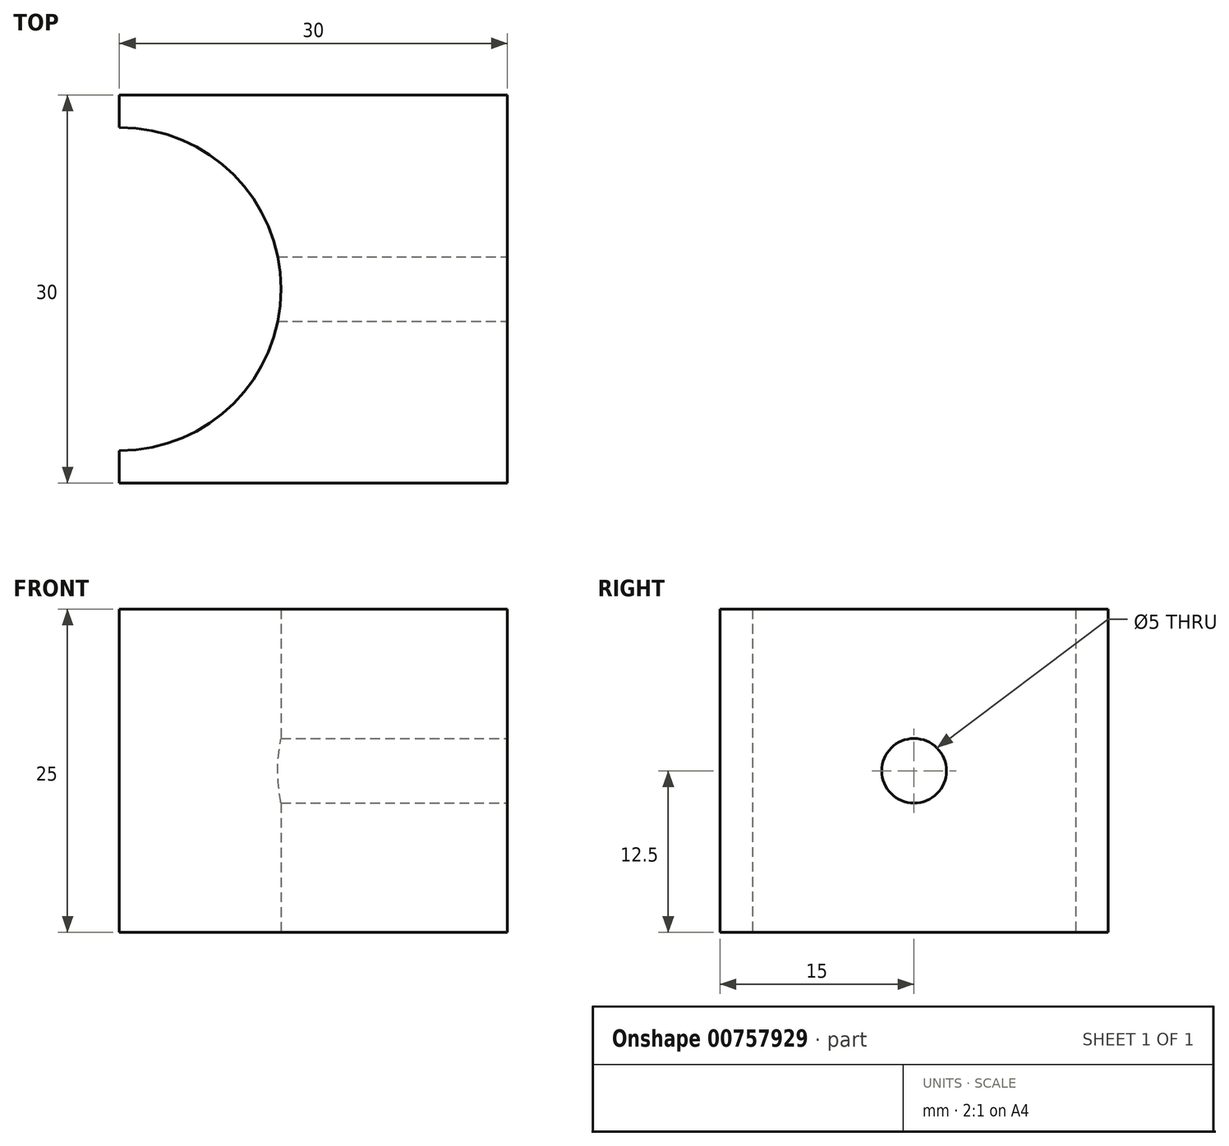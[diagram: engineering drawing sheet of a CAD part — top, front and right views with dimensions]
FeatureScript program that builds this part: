
annotation { "Feature Type Name" : "Feature", "Feature Type Description" : "" }
export const myFeature = defineFeature(function(context is Context, id is Id, definition is map)
    precondition{}
    {
        {
            var Q0;
            Q0=qCreatedBy(makeId("Top.planeOp"),FACE);
            var sketch = newSketch(context, id + "F0", { "sketchPlane" : qUnion([Q0])});
            skArc(sketch, "E0", {"start": v(0, -12.5) * mm, "mid": v(12.5, 0) * mm, "end": v(0, 12.5) * mm});
            skLineSegment(sketch, "E1", {"start": v(0, 15) * mm, "end": v(30, 15) * mm});
            skLineSegment(sketch, "E2", {"start": v(30, 15) * mm, "end": v(30, -15) * mm});
            skLineSegment(sketch, "E3", {"start": v(0, -15) * mm, "end": v(30, -15) * mm});
            skLineSegment(sketch, "E4", {"start": v(0, 15) * mm, "end": v(0, 12.5) * mm});
            skLineSegment(sketch, "E5", {"start": v(0, -15) * mm, "end": v(0, -12.5) * mm});
            skSolve(sketch);
        }
        {
            var Q0;
            Q0 = qSketchRegion(id + "F0", true);
            extrude(context, id + "F1", {"entities" : qUnion([Q0]), "depth" : 25 * mm, "offsetDistance" : 25 * mm});
        }
        {
            var Q0;
            Q0=makeQuery(id+"F1.opExtrude","SWEPT_FACE",FACE,{"disambiguationData":[OSD([sQuery(id+"F0.wireOp",EDGE,"E2")])]});
            var sketch = newSketch(context, id + "F2", { "sketchPlane" : qUnion([Q0])});
            skLineSegment(sketch, "E6", {"start": v(15, 25) * mm, "end": v(-15, 0) * mm, "construction": true});
            skPoint(sketch, "E7", {"position": v(0, 12.5) * mm});
            skSolve(sketch);
        }
        {
            var Q0;
            Q0=sQuery(id+"F2.wireOp",VERTEX,"E7");
            var Q1;
            Q1=makeQuery(id+"F1.opExtrude","SWEPT_BODY",BODY,{"disambiguationData":[OSD([sQuery(id+"F0.wireOp",EDGE,"E0"),sQuery(id+"F0.wireOp",EDGE,"E1"),sQuery(id+"F0.wireOp",EDGE,"E2"),sQuery(id+"F0.wireOp",EDGE,"E3"),sQuery(id+"F0.wireOp",EDGE,"E4"),sQuery(id+"F0.wireOp",EDGE,"E5")])]});
            hole(context, id + "F3", {"style" : HoleStyle.SIMPLE, "endStyle" : HoleEndStyle.THROUGH, "standardTappedOrClearance" : lookupTablePath({ "standard" : "ISO", "size" : "5", "type" : "Drilled" }), "standardBlindInLast" : lookupTablePath({ "standard" : "ISO", "size" : "5", "type" : "Drilled" }), "holeDiameter" : 5 * mm, "majorDiameter" : 5 * mm, "isTappedThrough" : true, "tappedDepth" : 12 * mm, "tapClearance" : 3, "locations" : qUnion([Q0]), "scope" : qUnion([Q1])});
        }
    });
